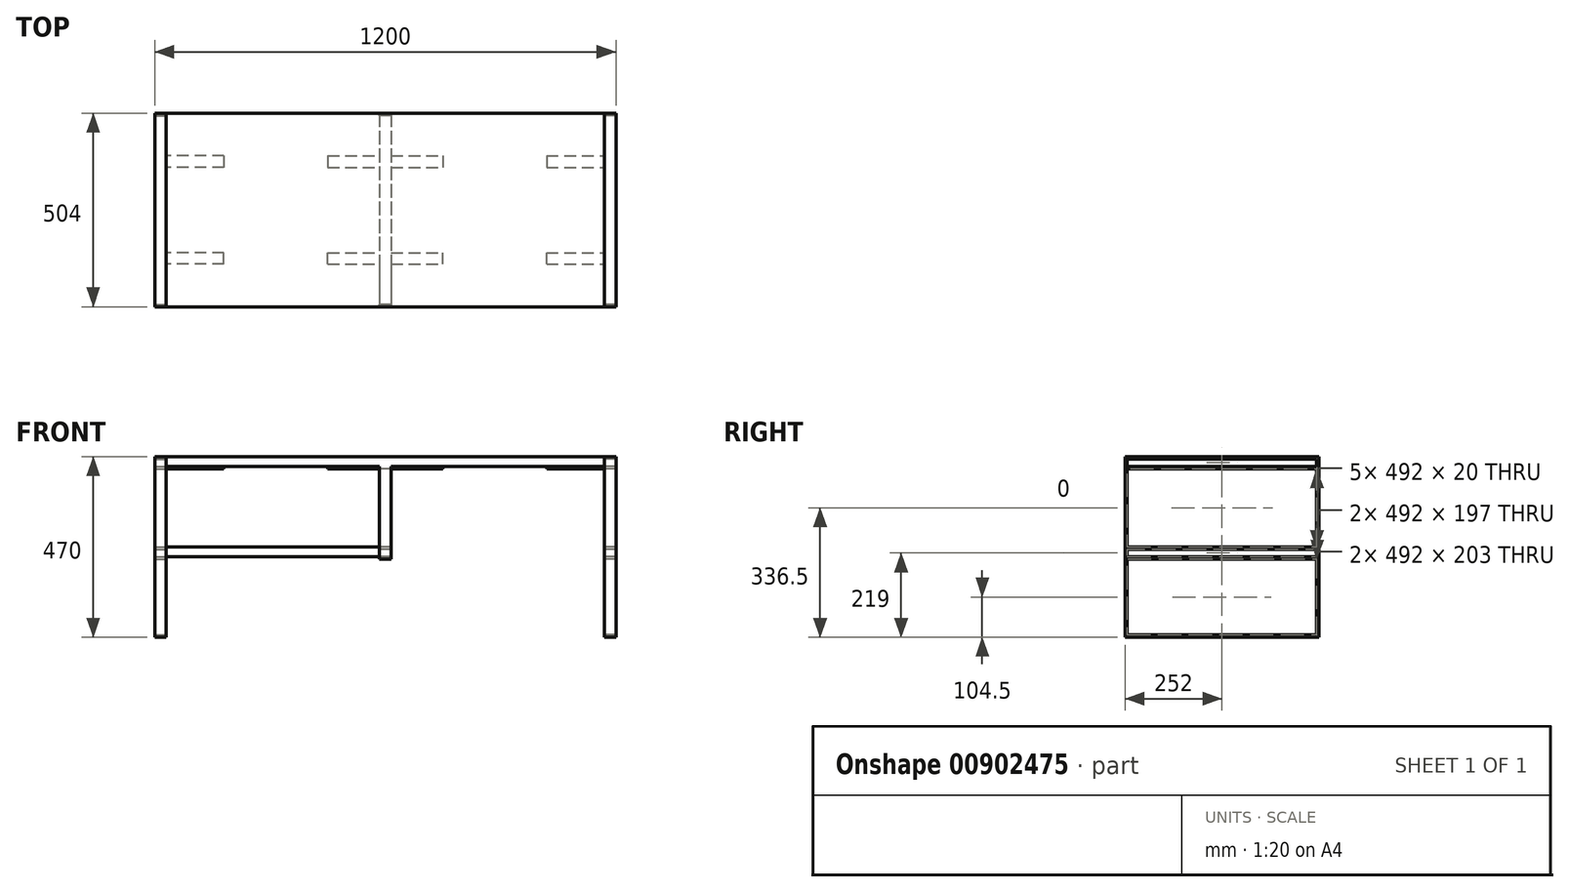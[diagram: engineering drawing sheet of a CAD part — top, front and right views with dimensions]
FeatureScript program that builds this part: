
annotation { "Feature Type Name" : "Feature", "Feature Type Description" : "" }
export const myFeature = defineFeature(function(context is Context, id is Id, definition is map)
    precondition{}
    {
        {
            assignVariable(context, id + "F0", {"variableType" : VariableType.LENGTH, "name" : "l", "lengthValue" : 1200 * mm});
        }
        {
            assignVariable(context, id + "F1", {"variableType" : VariableType.LENGTH, "name" : "t_eisen", "lengthValue" : 6 * mm});
        }
        {
            assignVariable(context, id + "F2", {"variableType" : VariableType.LENGTH, "name" : "b_eisen", "lengthValue" : 30 * mm});
        }
        {
            var Q0;
            Q0=qCreatedBy(makeId("Right.planeOp"),FACE);
            var sketch = newSketch(context, id + "F3", { "sketchPlane" : qUnion([Q0])});
            skLineSegment(sketch, "E0.bottom", {"start": v(-252, 470) * mm, "end": v(252, 470) * mm});
            skLineSegment(sketch, "E0.top", {"start": v(-252, 0) * mm, "end": v(252, 0) * mm});
            skLineSegment(sketch, "E0.left", {"start": v(-252, 470) * mm, "end": v(-252, 0) * mm});
            skLineSegment(sketch, "E0.right", {"start": v(252, 470) * mm, "end": v(252, 0) * mm});
            skLineSegment(sketch, "E1.bottom", {"start": v(246, 464) * mm, "end": v(-246, 464) * mm});
            skLineSegment(sketch, "E1.top", {"start": v(246, 6) * mm, "end": v(-246, 6) * mm});
            skLineSegment(sketch, "E1.left", {"start": v(246, 464) * mm, "end": v(246, 6) * mm});
            skLineSegment(sketch, "E1.right", {"start": v(-246, 464) * mm, "end": v(-246, 6) * mm});
            skLineSegment(sketch, "E2", {"start": v(0, 0) * mm, "end": v(0, 59.53) * mm, "construction": true});
            skLineSegment(sketch, "E3", {"start": v(246, 444) * mm, "end": v(-246, 444) * mm});
            skLineSegment(sketch, "E4", {"start": v(246, 438) * mm, "end": v(-246, 438) * mm});
            skLineSegment(sketch, "E5", {"start": v(246, 438) * mm, "end": v(252, 438) * mm});
            skLineSegment(sketch, "E6", {"start": v(-246, 438) * mm, "end": v(-252, 438) * mm});
            skLineSegment(sketch, "E7", {"start": v(246, 444) * mm, "end": v(252, 444) * mm});
            skLineSegment(sketch, "E8", {"start": v(-246, 444) * mm, "end": v(-252, 444) * mm});
            skLineSegment(sketch, "E9", {"start": v(252, 203) * mm, "end": v(-252, 203) * mm});
            skLineSegment(sketch, "E10", {"start": v(252, 209) * mm, "end": v(-252, 209) * mm});
            skLineSegment(sketch, "E11", {"start": v(246, 235) * mm, "end": v(-246, 235) * mm});
            skLineSegment(sketch, "E12", {"start": v(246, 235) * mm, "end": v(252, 235) * mm});
            skLineSegment(sketch, "E13", {"start": v(-246, 235) * mm, "end": v(-252, 235) * mm});
            skLineSegment(sketch, "E14", {"start": v(-246, 229) * mm, "end": v(246, 229) * mm});
            skSolve(sketch);
        }
        {
            var Q0;
            Q0=makeQuery(id+"F3.imprint","IMPRINT",FACE,{"disambiguationData":[TD([[makeQuery(id+"F3.imprint","IMPRINT",EDGE,{"derivedFrom":sQuery(id+"F3.wireOp",EDGE,"E0.bottom")}),-1.0]])]});
            var Q1;
            {var subQ0=sQuery(id+"F3.wireOp",EDGE,"E3");Q1=makeQuery(id+"F3.imprint","IMPRINT",FACE,{"disambiguationData":[TD([[makeQuery(id+"F3.imprint","IMPRINT",EDGE,{"derivedFrom":subQ0}),1.0]])]});}
            var Q2;
            {var subQ2=sQuery(id+"F3.wireOp",EDGE,"E0.top");Q2=makeQuery(id+"F3.imprint","IMPRINT",FACE,{"disambiguationData":[TD([[makeQuery(id+"F3.imprint","IMPRINT",EDGE,{"derivedFrom":subQ2}),1.0]])]});}
            var Q3;
            {var subQ0=sQuery(id+"F3.wireOp",EDGE,"E5");Q3=makeQuery(id+"F3.imprint","IMPRINT",FACE,{"disambiguationData":[TD([[makeQuery(id+"F3.imprint","IMPRINT",EDGE,{"derivedFrom":subQ0}),1.0]])]});}
            var Q4;
            {var subQ0=sQuery(id+"F3.wireOp",EDGE,"E6");Q4=makeQuery(id+"F3.imprint","IMPRINT",FACE,{"disambiguationData":[TD([[makeQuery(id+"F3.imprint","IMPRINT",EDGE,{"derivedFrom":subQ0}),-1.0]])]});}
            var Q5;
            {var subQ0=sQuery(id+"F3.wireOp",EDGE,"E5");Q5=makeQuery(id+"F3.imprint","IMPRINT",FACE,{"disambiguationData":[TD([[makeQuery(id+"F3.imprint","IMPRINT",EDGE,{"derivedFrom":subQ0}),-1.0]])]});}
            var Q6;
            {var subQ0=sQuery(id+"F3.wireOp",EDGE,"E9");var subQ1=sQuery(id+"F3.wireOp",EDGE,"E0.right");var subQ2=makeQuery(id+"F3.imprint","INTERSECT",VERTEX,{"derivedFrom":[subQ1,subQ0]});Q6=makeQuery(id+"F3.imprint","IMPRINT",FACE,{"disambiguationData":[TD([[makeQuery(id+"F3.imprint","IMPRINT",EDGE,{"disambiguationData":[TD([[subQ2,1.0]])],"derivedFrom":subQ1}),-1.0]])]});}
            var Q7;
            {var subQ0=sQuery(id+"F3.wireOp",EDGE,"E6");Q7=makeQuery(id+"F3.imprint","IMPRINT",FACE,{"disambiguationData":[TD([[makeQuery(id+"F3.imprint","IMPRINT",EDGE,{"derivedFrom":subQ0}),1.0]])]});}
            var Q8;
            {var subQ0=sQuery(id+"F3.wireOp",EDGE,"E9");var subQ1=sQuery(id+"F3.wireOp",EDGE,"E0.left");var subQ2=makeQuery(id+"F3.imprint","INTERSECT",VERTEX,{"derivedFrom":[subQ1,subQ0]});Q8=makeQuery(id+"F3.imprint","IMPRINT",FACE,{"disambiguationData":[TD([[makeQuery(id+"F3.imprint","IMPRINT",EDGE,{"disambiguationData":[TD([[subQ2,1.0]])],"derivedFrom":subQ1}),1.0]])]});}
            var Q9;
            {var subQ3=sQuery(id+"F3.wireOp",EDGE,"E13");Q9=makeQuery(id+"F3.imprint","IMPRINT",FACE,{"disambiguationData":[TD([[makeQuery(id+"F3.imprint","IMPRINT",EDGE,{"derivedFrom":subQ3}),1.0]])]});}
            var Q10;
            {var subQ3=sQuery(id+"F3.wireOp",EDGE,"E12");Q10=makeQuery(id+"F3.imprint","IMPRINT",FACE,{"disambiguationData":[TD([[makeQuery(id+"F3.imprint","IMPRINT",EDGE,{"derivedFrom":subQ3}),-1.0]])]});}
            extrude(context, id + "F4", {"entities" : qUnion([Q0, Q1, Q2, Q3, Q4, Q5, Q6, Q7, Q8, Q9, Q10]), "oppositeDirection" : true, "depth" : getVariable(context, 'l') / 2, "offsetDistance" : 25 * mm, "hasSecondDirection" : true, "secondDirectionOppositeDirection" : true, "secondDirectionDepth" : getVariable(context, 'l') / 2 - getVariable(context, 'b_eisen')});
        }
        {
            var Q0;
            {var subQ3=sQuery(id+"F3.wireOp",EDGE,"E0.bottom");Q0=makeQuery(id+"F3.imprint","IMPRINT",FACE,{"disambiguationData":[TD([[makeQuery(id+"F3.imprint","IMPRINT",EDGE,{"derivedFrom":subQ3}),-1.0]])]});}
            var Q1;
            {var subQ0=sQuery(id+"F3.wireOp",EDGE,"E1.bottom");Q1=makeQuery(id+"F3.imprint","IMPRINT",FACE,{"disambiguationData":[TD([[makeQuery(id+"F3.imprint","IMPRINT",EDGE,{"derivedFrom":subQ0}),1.0]])]});}
            extrude(context, id + "F5", {"entities" : qUnion([Q0, Q1]), "oppositeDirection" : true, "depth" : getVariable(context, 'l') / 2, "offsetDistance" : 25 * mm});
        }
        {
            var Q0;
            Q0=makeQuery(id+"F4.opExtrude","SWEPT_BODY",BODY,{"disambiguationData":[OSD([sQuery(id+"F3.wireOp",EDGE,"E0.bottom"),sQuery(id+"F3.wireOp",EDGE,"E0.top"),sQuery(id+"F3.wireOp",EDGE,"E0.left"),sQuery(id+"F3.wireOp",EDGE,"E0.right"),sQuery(id+"F3.wireOp",EDGE,"E1.bottom"),sQuery(id+"F3.wireOp",EDGE,"E1.top"),sQuery(id+"F3.wireOp",EDGE,"E1.left"),sQuery(id+"F3.wireOp",EDGE,"E1.right"),sQuery(id+"F3.wireOp",EDGE,"E3"),sQuery(id+"F3.wireOp",EDGE,"E4")])]});
            var Q1;
            Q1=makeQuery(id+"F5.opExtrude","SWEPT_BODY",BODY,{"disambiguationData":[OSD([sQuery(id+"F3.wireOp",EDGE,"E0.bottom"),sQuery(id+"F3.wireOp",EDGE,"E0.left"),sQuery(id+"F3.wireOp",EDGE,"E0.right"),sQuery(id+"F3.wireOp",EDGE,"E3"),sQuery(id+"F3.wireOp",EDGE,"E7"),sQuery(id+"F3.wireOp",EDGE,"E8")])]});
            booleanBodies(context, id + "F6", {"operationType" : BooleanOperationType.SUBTRACTION, "tools" : qUnion([Q0]), "targets" : qUnion([Q1]), "keepTools" : true});
        }
        {
            var Q0;
            Q0=makeQuery(id+"F5.opExtrude","SWEPT_BODY",BODY,{"disambiguationData":[OSD([sQuery(id+"F3.wireOp",EDGE,"E0.bottom"),sQuery(id+"F3.wireOp",EDGE,"E0.left"),sQuery(id+"F3.wireOp",EDGE,"E0.right"),sQuery(id+"F3.wireOp",EDGE,"E3"),sQuery(id+"F3.wireOp",EDGE,"E7"),sQuery(id+"F3.wireOp",EDGE,"E8")])]});
            var Q1;
            Q1=makeQuery(id+"F4.opExtrude","SWEPT_BODY",BODY,{"disambiguationData":[OSD([sQuery(id+"F3.wireOp",EDGE,"E0.bottom"),sQuery(id+"F3.wireOp",EDGE,"E0.top"),sQuery(id+"F3.wireOp",EDGE,"E0.left"),sQuery(id+"F3.wireOp",EDGE,"E0.right"),sQuery(id+"F3.wireOp",EDGE,"E1.bottom"),sQuery(id+"F3.wireOp",EDGE,"E1.top"),sQuery(id+"F3.wireOp",EDGE,"E1.left"),sQuery(id+"F3.wireOp",EDGE,"E1.right"),sQuery(id+"F3.wireOp",EDGE,"E3"),sQuery(id+"F3.wireOp",EDGE,"E4")])]});
            var Q2;
            Q2=qCreatedBy(makeId("Right.planeOp"),FACE);
            mirror(context, id + "F7", {"entities" : qUnion([Q0, Q1]), "mirrorPlane" : qUnion([Q2])});
        }
        {
            var Q0;
            Q0=makeQuery(id+"F7.opPattern","COPY",BODY,{"derivedFrom":makeQuery(id+"F5.opExtrude","SWEPT_BODY",BODY,{"disambiguationData":[OSD([sQuery(id+"F3.wireOp",EDGE,"E0.bottom"),sQuery(id+"F3.wireOp",EDGE,"E0.left"),sQuery(id+"F3.wireOp",EDGE,"E0.right"),sQuery(id+"F3.wireOp",EDGE,"E3"),sQuery(id+"F3.wireOp",EDGE,"E7"),sQuery(id+"F3.wireOp",EDGE,"E8")])]}),"instanceName":"1"});
            var Q1;
            Q1=makeQuery(id+"F5.opExtrude","SWEPT_BODY",BODY,{"disambiguationData":[OSD([sQuery(id+"F3.wireOp",EDGE,"E0.bottom"),sQuery(id+"F3.wireOp",EDGE,"E0.left"),sQuery(id+"F3.wireOp",EDGE,"E0.right"),sQuery(id+"F3.wireOp",EDGE,"E3"),sQuery(id+"F3.wireOp",EDGE,"E7"),sQuery(id+"F3.wireOp",EDGE,"E8")])]});
            booleanBodies(context, id + "F8", {"operationType" : BooleanOperationType.UNION, "tools" : qUnion([Q0, Q1])});
        }
        {
            var Q0;
            {var subQ0=sQuery(id+"F3.wireOp",EDGE,"E11");Q0=makeQuery(id+"F3.imprint","IMPRINT",FACE,{"disambiguationData":[TD([[makeQuery(id+"F3.imprint","IMPRINT",EDGE,{"derivedFrom":subQ0}),1.0]])]});}
            var Q1;
            {var subQ0=sQuery(id+"F3.wireOp",EDGE,"E10");var subQ1=sQuery(id+"F3.wireOp",EDGE,"E1.left");var subQ2=makeQuery(id+"F3.imprint","INTERSECT",VERTEX,{"derivedFrom":[subQ1,subQ0]});Q1=makeQuery(id+"F3.imprint","IMPRINT",FACE,{"disambiguationData":[TD([[makeQuery(id+"F3.imprint","IMPRINT",EDGE,{"disambiguationData":[TD([[subQ2,-1.0]])],"derivedFrom":subQ1}),-1.0]])]});}
            var Q2;
            {var subQ6=sQuery(id+"F3.wireOp",EDGE,"E13");Q2=makeQuery(id+"F3.imprint","IMPRINT",FACE,{"disambiguationData":[TD([[makeQuery(id+"F3.imprint","IMPRINT",EDGE,{"derivedFrom":subQ6}),1.0]])]});}
            var Q3;
            {var subQ0=sQuery(id+"F3.wireOp",EDGE,"E9");var subQ1=sQuery(id+"F3.wireOp",EDGE,"E0.left");var subQ2=makeQuery(id+"F3.imprint","INTERSECT",VERTEX,{"derivedFrom":[subQ1,subQ0]});Q3=makeQuery(id+"F3.imprint","IMPRINT",FACE,{"disambiguationData":[TD([[makeQuery(id+"F3.imprint","IMPRINT",EDGE,{"disambiguationData":[TD([[subQ2,1.0]])],"derivedFrom":subQ1}),1.0]])]});}
            var Q4;
            {var subQ0=sQuery(id+"F3.wireOp",EDGE,"E6");Q4=makeQuery(id+"F3.imprint","IMPRINT",FACE,{"disambiguationData":[TD([[makeQuery(id+"F3.imprint","IMPRINT",EDGE,{"derivedFrom":subQ0}),1.0]])]});}
            var Q5;
            {var subQ0=sQuery(id+"F3.wireOp",EDGE,"E6");Q5=makeQuery(id+"F3.imprint","IMPRINT",FACE,{"disambiguationData":[TD([[makeQuery(id+"F3.imprint","IMPRINT",EDGE,{"derivedFrom":subQ0}),-1.0]])]});}
            var Q6;
            {var subQ0=sQuery(id+"F3.wireOp",EDGE,"E3");Q6=makeQuery(id+"F3.imprint","IMPRINT",FACE,{"disambiguationData":[TD([[makeQuery(id+"F3.imprint","IMPRINT",EDGE,{"derivedFrom":subQ0}),1.0]])]});}
            var Q7;
            {var subQ0=sQuery(id+"F3.wireOp",EDGE,"E5");Q7=makeQuery(id+"F3.imprint","IMPRINT",FACE,{"disambiguationData":[TD([[makeQuery(id+"F3.imprint","IMPRINT",EDGE,{"derivedFrom":subQ0}),-1.0]])]});}
            var Q8;
            {var subQ6=sQuery(id+"F3.wireOp",EDGE,"E12");Q8=makeQuery(id+"F3.imprint","IMPRINT",FACE,{"disambiguationData":[TD([[makeQuery(id+"F3.imprint","IMPRINT",EDGE,{"derivedFrom":subQ6}),-1.0]])]});}
            var Q9;
            {var subQ0=sQuery(id+"F3.wireOp",EDGE,"E9");var subQ1=sQuery(id+"F3.wireOp",EDGE,"E0.right");var subQ2=makeQuery(id+"F3.imprint","INTERSECT",VERTEX,{"derivedFrom":[subQ1,subQ0]});Q9=makeQuery(id+"F3.imprint","IMPRINT",FACE,{"disambiguationData":[TD([[makeQuery(id+"F3.imprint","IMPRINT",EDGE,{"disambiguationData":[TD([[subQ2,1.0]])],"derivedFrom":subQ1}),-1.0]])]});}
            var Q10;
            {var subQ0=sQuery(id+"F3.wireOp",EDGE,"E5");Q10=makeQuery(id+"F3.imprint","IMPRINT",FACE,{"disambiguationData":[TD([[makeQuery(id+"F3.imprint","IMPRINT",EDGE,{"derivedFrom":subQ0}),1.0]])]});}
            extrude(context, id + "F9", {"entities" : qUnion([Q0, Q1, Q2, Q3, Q4, Q5, Q6, Q7, Q8, Q9, Q10]), "depth" : getVariable(context, 'b_eisen'), "offsetDistance" : 25 * mm, "symmetric" : true});
        }
        {
            var Q0;
            {var subQ0=sQuery(id+"F3.wireOp",EDGE,"E10");var subQ1=sQuery(id+"F3.wireOp",EDGE,"E1.left");var subQ2=makeQuery(id+"F3.imprint","INTERSECT",VERTEX,{"derivedFrom":[subQ1,subQ0]});Q0=makeQuery(id+"F3.imprint","IMPRINT",FACE,{"disambiguationData":[TD([[makeQuery(id+"F3.imprint","IMPRINT",EDGE,{"disambiguationData":[TD([[subQ2,-1.0]])],"derivedFrom":subQ1}),-1.0]])]});}
            var Q1;
            {var subQ0=sQuery(id+"F3.wireOp",EDGE,"E11");Q1=makeQuery(id+"F3.imprint","IMPRINT",FACE,{"disambiguationData":[TD([[makeQuery(id+"F3.imprint","IMPRINT",EDGE,{"derivedFrom":subQ0}),1.0]])]});}
            extrude(context, id + "F10", {"entities" : qUnion([Q0, Q1]), "operationType" : NewBodyOperationType.ADD, "oppositeDirection" : true, "depth" : getVariable(context, 'l') / 2, "offsetDistance" : 25 * mm, "hasSecondDirection" : true, "secondDirectionOppositeDirection" : true, "secondDirectionDepth" : getVariable(context, 'l') / 2 - getVariable(context, 'b_eisen')});
        }
        {
            var Q0;
            {var subQ0=sQuery(id+"F3.wireOp",EDGE,"E11");Q0=makeQuery(id+"F3.imprint","IMPRINT",FACE,{"disambiguationData":[TD([[makeQuery(id+"F3.imprint","IMPRINT",EDGE,{"derivedFrom":subQ0}),1.0]])]});}
            var Q1;
            {var subQ3=sQuery(id+"F3.wireOp",EDGE,"E13");Q1=makeQuery(id+"F3.imprint","IMPRINT",FACE,{"disambiguationData":[TD([[makeQuery(id+"F3.imprint","IMPRINT",EDGE,{"derivedFrom":subQ3}),1.0]])]});}
            var Q2;
            {var subQ3=sQuery(id+"F3.wireOp",EDGE,"E12");Q2=makeQuery(id+"F3.imprint","IMPRINT",FACE,{"disambiguationData":[TD([[makeQuery(id+"F3.imprint","IMPRINT",EDGE,{"derivedFrom":subQ3}),-1.0]])]});}
            var Q3;
            {var subQ0=sQuery(id+"F3.wireOp",EDGE,"E14");Q3=makeQuery(id+"F3.imprint","IMPRINT",FACE,{"disambiguationData":[TD([[makeQuery(id+"F3.imprint","IMPRINT",EDGE,{"derivedFrom":subQ0}),-1.0]])]});}
            extrude(context, id + "F11", {"entities" : qUnion([Q0, Q1, Q2, Q3]), "oppositeDirection" : true, "depth" : getVariable(context, 'l') / 2, "offsetDistance" : 25 * mm, "hasSecondDirection" : true, "secondDirectionOppositeDirection" : false, "secondDirectionDepth" : getVariable(context, 'b_eisen') / 2});
        }
        {
            var Q0;
            Q0=makeQuery(id+"F9.opExtrude","SWEPT_BODY",BODY,{"disambiguationData":[OSD([sQuery(id+"F3.wireOp",EDGE,"E0.bottom"),sQuery(id+"F3.wireOp",EDGE,"E0.left"),sQuery(id+"F3.wireOp",EDGE,"E0.right"),sQuery(id+"F3.wireOp",EDGE,"E1.bottom"),sQuery(id+"F3.wireOp",EDGE,"E1.left"),sQuery(id+"F3.wireOp",EDGE,"E1.right"),sQuery(id+"F3.wireOp",EDGE,"E9"),sQuery(id+"F3.wireOp",EDGE,"E10")])]});
            var Q1;
            Q1=makeQuery(id+"F4.opExtrude","SWEPT_BODY",BODY,{"disambiguationData":[OSD([sQuery(id+"F3.wireOp",EDGE,"E0.bottom"),sQuery(id+"F3.wireOp",EDGE,"E0.top"),sQuery(id+"F3.wireOp",EDGE,"E0.left"),sQuery(id+"F3.wireOp",EDGE,"E0.right"),sQuery(id+"F3.wireOp",EDGE,"E1.bottom"),sQuery(id+"F3.wireOp",EDGE,"E1.top"),sQuery(id+"F3.wireOp",EDGE,"E1.left"),sQuery(id+"F3.wireOp",EDGE,"E1.right"),sQuery(id+"F3.wireOp",EDGE,"E3"),sQuery(id+"F3.wireOp",EDGE,"E4")])]});
            var Q2;
            Q2=makeQuery(id+"F11.opExtrude","SWEPT_BODY",BODY,{"disambiguationData":[OSD([sQuery(id+"F3.wireOp",EDGE,"E0.left"),sQuery(id+"F3.wireOp",EDGE,"E0.right"),sQuery(id+"F3.wireOp",EDGE,"E10"),sQuery(id+"F3.wireOp",EDGE,"E11"),sQuery(id+"F3.wireOp",EDGE,"E12"),sQuery(id+"F3.wireOp",EDGE,"E13")])]});
            booleanBodies(context, id + "F12", {"operationType" : BooleanOperationType.SUBTRACTION, "tools" : qUnion([Q0, Q1]), "targets" : qUnion([Q2]), "keepTools" : true});
        }
        {
            var Q0;
            {var subQ0=sQuery(id+"F3.wireOp",EDGE,"E10");var subQ1=sQuery(id+"F3.wireOp",EDGE,"E1.left");var subQ2=makeQuery(id+"F3.imprint","INTERSECT",VERTEX,{"derivedFrom":[subQ1,subQ0]});Q0=makeQuery(id+"F3.imprint","IMPRINT",FACE,{"disambiguationData":[TD([[makeQuery(id+"F3.imprint","IMPRINT",EDGE,{"disambiguationData":[TD([[subQ2,-1.0]])],"derivedFrom":subQ1}),-1.0]])]});}
            var Q1;
            {var subQ0=sQuery(id+"F3.wireOp",EDGE,"E11");Q1=makeQuery(id+"F3.imprint","IMPRINT",FACE,{"disambiguationData":[TD([[makeQuery(id+"F3.imprint","IMPRINT",EDGE,{"derivedFrom":subQ0}),1.0]])]});}
            extrude(context, id + "F13", {"entities" : qUnion([Q0, Q1]), "operationType" : NewBodyOperationType.ADD, "depth" : getVariable(context, 'l') / 2, "offsetDistance" : 25 * mm, "hasSecondDirection" : true, "secondDirectionOppositeDirection" : false, "secondDirectionDepth" : getVariable(context, 'l') / 2 - getVariable(context, 'b_eisen')});
        }
        {
            var Q0;
            Q0=makeQuery(id+"F9.opExtrude","SWEPT_BODY",BODY,{"disambiguationData":[OSD([sQuery(id+"F3.wireOp",EDGE,"E0.left"),sQuery(id+"F3.wireOp",EDGE,"E0.right"),sQuery(id+"F3.wireOp",EDGE,"E1.left"),sQuery(id+"F3.wireOp",EDGE,"E1.right"),sQuery(id+"F3.wireOp",EDGE,"E3"),sQuery(id+"F3.wireOp",EDGE,"E4"),sQuery(id+"F3.wireOp",EDGE,"E7"),sQuery(id+"F3.wireOp",EDGE,"E8"),sQuery(id+"F3.wireOp",EDGE,"E9"),sQuery(id+"F3.wireOp",EDGE,"E10")])]});
            var Q1;
            Q1=makeQuery(id+"F4.opExtrude","SWEPT_BODY",BODY,{"disambiguationData":[OSD([sQuery(id+"F3.wireOp",EDGE,"E0.bottom"),sQuery(id+"F3.wireOp",EDGE,"E0.top"),sQuery(id+"F3.wireOp",EDGE,"E0.left"),sQuery(id+"F3.wireOp",EDGE,"E0.right"),sQuery(id+"F3.wireOp",EDGE,"E1.bottom"),sQuery(id+"F3.wireOp",EDGE,"E1.top"),sQuery(id+"F3.wireOp",EDGE,"E1.left"),sQuery(id+"F3.wireOp",EDGE,"E1.right"),sQuery(id+"F3.wireOp",EDGE,"E3"),sQuery(id+"F3.wireOp",EDGE,"E4")])]});
            var Q2;
            Q2=makeQuery(id+"F11.opExtrude","SWEPT_BODY",BODY,{"disambiguationData":[OSD([sQuery(id+"F3.wireOp",EDGE,"E0.left"),sQuery(id+"F3.wireOp",EDGE,"E0.right"),sQuery(id+"F3.wireOp",EDGE,"E10"),sQuery(id+"F3.wireOp",EDGE,"E11"),sQuery(id+"F3.wireOp",EDGE,"E12"),sQuery(id+"F3.wireOp",EDGE,"E13")])]});
            booleanBodies(context, id + "F14", {"operationType" : BooleanOperationType.SUBTRACTION, "tools" : qUnion([Q0, Q1]), "targets" : qUnion([Q2]), "keepTools" : true});
        }
        {
            var Q0;
            {var subQ0=makeQuery(id+"F5.opExtrude","SWEPT_FACE",FACE,{"disambiguationData":[OSD([sQuery(id+"F3.wireOp",EDGE,"E3"),sQuery(id+"F3.wireOp",EDGE,"E7"),sQuery(id+"F3.wireOp",EDGE,"E8")])]});Q0=makeQuery(id+"F8.opBoolean","MERGE",FACE,{"derivedFrom":[subQ0,makeQuery(id+"F7.opPattern","COPY",FACE,{"derivedFrom":subQ0,"instanceName":"1"})]});}
            var sketch = newSketch(context, id + "F15", { "sketchPlane" : qUnion([Q0])});
            skLineSegment(sketch, "E15.bottom", {"start": v(420, 141) * mm, "end": v(570, 141) * mm});
            skLineSegment(sketch, "E15.top", {"start": v(420, 111) * mm, "end": v(570, 111) * mm});
            skLineSegment(sketch, "E15.left", {"start": v(420, 141) * mm, "end": v(420, 111) * mm});
            skLineSegment(sketch, "E15.right", {"start": v(570, 141) * mm, "end": v(570, 111) * mm});
            skSolve(sketch);
        }
        {
            var Q0;
            Q0=makeQuery(id+"F15.imprint","IMPRINT",FACE,{"disambiguationData":[TD([[makeQuery(id+"F15.imprint","IMPRINT",EDGE,{"derivedFrom":sQuery(id+"F15.wireOp",EDGE,"E15.bottom")}),-1.0]])]});
            extrude(context, id + "F16", {"entities" : qUnion([Q0]), "depth" : getVariable(context, 't_eisen'), "offsetDistance" : 25 * mm});
        }
        {
            var Q0;
            Q0=makeQuery(id+"F16.opExtrude","SWEPT_BODY",BODY,{"disambiguationData":[OSD([sQuery(id+"F15.wireOp",EDGE,"E15.bottom"),sQuery(id+"F15.wireOp",EDGE,"E15.top"),sQuery(id+"F15.wireOp",EDGE,"E15.left"),sQuery(id+"F15.wireOp",EDGE,"E15.right")])]});
            var Q1;
            Q1=qCreatedBy(makeId("Front.planeOp"),FACE);
            mirror(context, id + "F17", {"entities" : qUnion([Q0]), "mirrorPlane" : qUnion([Q1])});
        }
        {
            var Q0;
            Q0=makeQuery(id+"F16.opExtrude","SWEPT_BODY",BODY,{"disambiguationData":[OSD([sQuery(id+"F15.wireOp",EDGE,"E15.bottom"),sQuery(id+"F15.wireOp",EDGE,"E15.top"),sQuery(id+"F15.wireOp",EDGE,"E15.left"),sQuery(id+"F15.wireOp",EDGE,"E15.right")])]});
            var Q1;
            Q1=makeQuery(id+"F17.opPattern","COPY",BODY,{"derivedFrom":makeQuery(id+"F16.opExtrude","SWEPT_BODY",BODY,{"disambiguationData":[OSD([sQuery(id+"F15.wireOp",EDGE,"E15.bottom"),sQuery(id+"F15.wireOp",EDGE,"E15.top"),sQuery(id+"F15.wireOp",EDGE,"E15.left"),sQuery(id+"F15.wireOp",EDGE,"E15.right")])]}),"instanceName":"1"});
            var Q2;
            Q2=qCreatedBy(makeId("Right.planeOp"),FACE);
            mirror(context, id + "F18", {"entities" : qUnion([Q0, Q1]), "mirrorPlane" : qUnion([Q2])});
        }
        {
            var Q0;
            Q0=makeQuery(id+"F16.opExtrude","SWEPT_BODY",BODY,{"disambiguationData":[OSD([sQuery(id+"F15.wireOp",EDGE,"E15.bottom"),sQuery(id+"F15.wireOp",EDGE,"E15.top"),sQuery(id+"F15.wireOp",EDGE,"E15.left"),sQuery(id+"F15.wireOp",EDGE,"E15.right")])]});
            var Q1;
            Q1=makeQuery(id+"F17.opPattern","COPY",BODY,{"derivedFrom":makeQuery(id+"F16.opExtrude","SWEPT_BODY",BODY,{"disambiguationData":[OSD([sQuery(id+"F15.wireOp",EDGE,"E15.bottom"),sQuery(id+"F15.wireOp",EDGE,"E15.top"),sQuery(id+"F15.wireOp",EDGE,"E15.left"),sQuery(id+"F15.wireOp",EDGE,"E15.right")])]}),"instanceName":"1"});
            var Q2;
            Q2=makeQuery(id+"F16.opExtrude","CAP_EDGE",EDGE,{"disambiguationData":[OSD([sQuery(id+"F15.wireOp",EDGE,"E15.bottom")])],"isStart":true});
            transform(context, id + "F19", {"entities" : qUnion([Q0, Q1]), "transformType" : TransformType.TRANSLATION_DISTANCE, "transformDirection" : qUnion([Q2]), "distance" : getVariable(context, 'l') / 2 - getVariable(context, 'b_eisen') - 150 * mm, "oppositeDirection" : true, "makeCopy" : true});
        }
        {
            var Q0;
            Q0=makeQuery(id+"F19.opPattern","COPY",BODY,{"derivedFrom":makeQuery(id+"F16.opExtrude","SWEPT_BODY",BODY,{"disambiguationData":[OSD([sQuery(id+"F15.wireOp",EDGE,"E15.bottom"),sQuery(id+"F15.wireOp",EDGE,"E15.top"),sQuery(id+"F15.wireOp",EDGE,"E15.left"),sQuery(id+"F15.wireOp",EDGE,"E15.right")])]}),"instanceName":"1"});
            var Q1;
            Q1=makeQuery(id+"F19.opPattern","COPY",BODY,{"derivedFrom":makeQuery(id+"F17.opPattern","COPY",BODY,{"derivedFrom":makeQuery(id+"F16.opExtrude","SWEPT_BODY",BODY,{"disambiguationData":[OSD([sQuery(id+"F15.wireOp",EDGE,"E15.bottom"),sQuery(id+"F15.wireOp",EDGE,"E15.top"),sQuery(id+"F15.wireOp",EDGE,"E15.left"),sQuery(id+"F15.wireOp",EDGE,"E15.right")])]}),"instanceName":"1"}),"instanceName":"1"});
            var Q2;
            Q2=qCreatedBy(makeId("Right.planeOp"),FACE);
            mirror(context, id + "F20", {"operationType" : NewBodyOperationType.ADD, "entities" : qUnion([Q0, Q1]), "mirrorPlane" : qUnion([Q2])});
        }
    });
